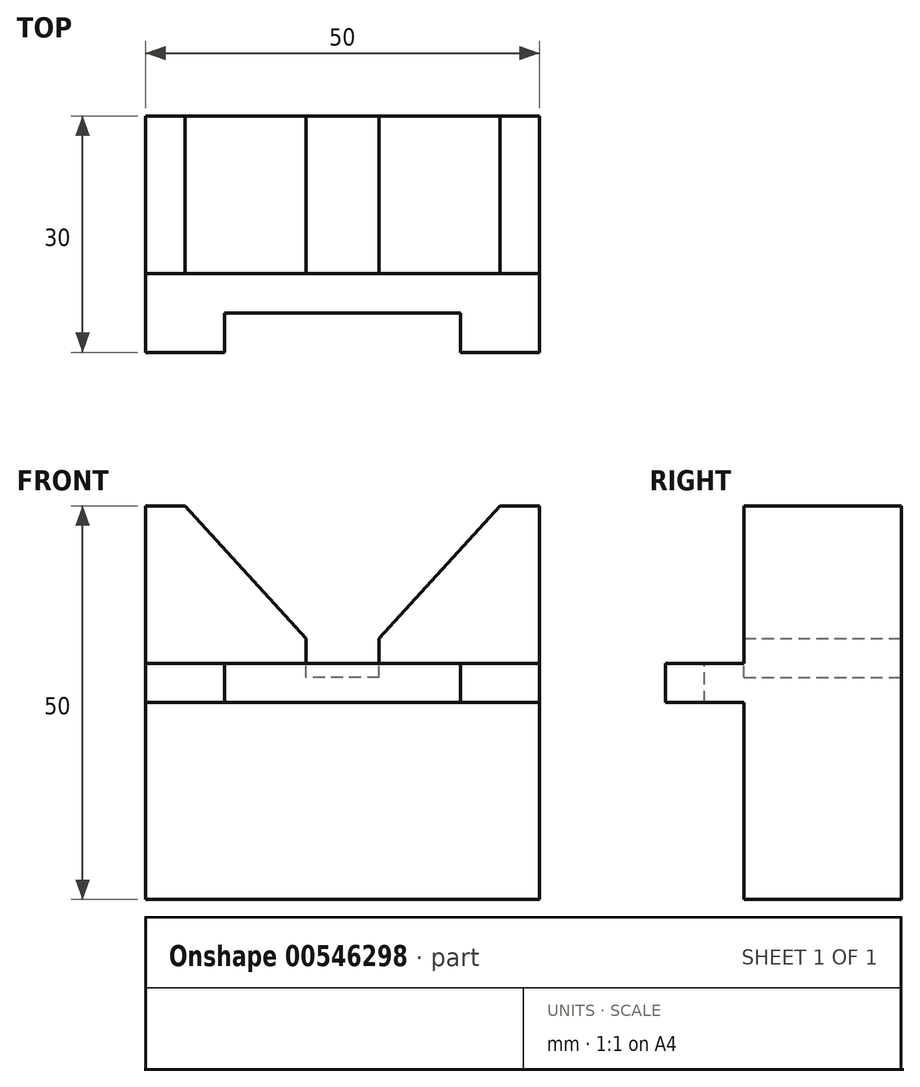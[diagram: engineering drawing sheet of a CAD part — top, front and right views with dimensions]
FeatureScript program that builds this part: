
annotation { "Feature Type Name" : "Feature", "Feature Type Description" : "" }
export const myFeature = defineFeature(function(context is Context, id is Id, definition is map)
    precondition{}
    {
        {
            var Q0;
            Q0=qCreatedBy(makeId("Top.planeOp"),FACE);
            var sketch = newSketch(context, id + "F0", { "sketchPlane" : qUnion([Q0])});
            skLineSegment(sketch, "E0.bottom", {"start": v(25, -15) * mm, "end": v(-25, -15) * mm});
            skLineSegment(sketch, "E0.top", {"start": v(25, 15) * mm, "end": v(-25, 15) * mm});
            skLineSegment(sketch, "E0.left", {"start": v(25, -15) * mm, "end": v(25, 15) * mm});
            skLineSegment(sketch, "E0.right", {"start": v(-25, -15) * mm, "end": v(-25, 15) * mm});
            skPoint(sketch, "E0.middle", {"position": v(0, 0) * mm});
            skSolve(sketch);
        }
        {
            var Q0;
            Q0 = qSketchRegion(id + "F0", true);
            extrude(context, id + "F1", {"entities" : qUnion([Q0]), "depth" : 50 * mm, "offsetDistance" : 25 * mm});
        }
        {
            var Q0;
            Q0=makeQuery(id+"F1.opExtrude","CAP_FACE",FACE,{"disambiguationData":[OSD([sQuery(id+"F0.wireOp",EDGE,"E0.bottom"),sQuery(id+"F0.wireOp",EDGE,"E0.top"),sQuery(id+"F0.wireOp",EDGE,"E0.left"),sQuery(id+"F0.wireOp",EDGE,"E0.right")])],"isStart":false});
            var sketch = newSketch(context, id + "F2", { "sketchPlane" : qUnion([Q0])});
            skLineSegment(sketch, "E1", {"start": v(-15, -15) * mm, "end": v(-15, -10) * mm});
            skLineSegment(sketch, "E2", {"start": v(-15, -10) * mm, "end": v(15, -10) * mm});
            skLineSegment(sketch, "E3", {"start": v(15, -10) * mm, "end": v(15, -15) * mm});
            skLineSegment(sketch, "E4", {"start": v(-25, -5) * mm, "end": v(25, -5) * mm});
            skSolve(sketch);
        }
        {
            var Q0;
            {var subQ2=sQuery(id+"F2.wireOp",EDGE,"E1");Q0=makeQuery(id+"F2.imprint","IMPRINT",FACE,{"disambiguationData":[TD([[makeQuery(id+"F2.imprint","IMPRINT",EDGE,{"derivedFrom":subQ2}),1.0]])]});}
            extrude(context, id + "F3", {"entities" : qUnion([Q0]), "operationType" : NewBodyOperationType.REMOVE, "oppositeDirection" : true, "depth" : 20 * mm, "offsetDistance" : 25 * mm});
        }
        {
            var Q0;
            {var subQ0=sQuery(id+"F0.wireOp",EDGE,"E0.bottom");Q0=makeQuery(id+"F3.boolean.opBoolean","SPLIT",FACE,{"disambiguationData":[TD([makeQuery(id+"F1.opExtrude","SWEPT_FACE",FACE,{"disambiguationData":[OSD([subQ0])]})])],"derivedFrom":makeQuery(id+"F1.opExtrude","CAP_FACE",FACE,{"disambiguationData":[OSD([subQ0,sQuery(id+"F0.wireOp",EDGE,"E0.top"),sQuery(id+"F0.wireOp",EDGE,"E0.left"),sQuery(id+"F0.wireOp",EDGE,"E0.right")])],"isStart":false})});}
            extrude(context, id + "F4", {"entities" : qUnion([Q0]), "operationType" : NewBodyOperationType.REMOVE, "endBound" : BoundingType.THROUGH_ALL, "oppositeDirection" : true, "depth" : 25 * mm, "offsetDistance" : 25 * mm});
        }
        {
            var Q0;
            Q0=makeQuery(id+"F1.opExtrude","CAP_FACE",FACE,{"disambiguationData":[OSD([sQuery(id+"F0.wireOp",EDGE,"E0.bottom"),sQuery(id+"F0.wireOp",EDGE,"E0.top"),sQuery(id+"F0.wireOp",EDGE,"E0.left"),sQuery(id+"F0.wireOp",EDGE,"E0.right")])],"isStart":true});
            var sketch = newSketch(context, id + "F5", { "sketchPlane" : qUnion([Q0])});
            skLineSegment(sketch, "E5", {"start": v(-25, 5) * mm, "end": v(25, 5) * mm});
            skSolve(sketch);
        }
        {
            var Q0;
            Q0 = qSketchRegion(id + "F5", true);
            var Q1;
            {var subQ6=sQuery(id+"F5.wireOp",EDGE,"E5");Q1=makeQuery(id+"F5.imprint","IMPRINT",FACE,{"disambiguationData":[TD([[makeQuery(id+"F5.imprint","IMPRINT",EDGE,{"derivedFrom":subQ6}),1.0]])]});}
            extrude(context, id + "F6", {"entities" : qUnion([Q0, Q1]), "operationType" : NewBodyOperationType.REMOVE, "oppositeDirection" : true, "depth" : 25 * mm, "offsetDistance" : 25 * mm});
        }
        {
            var Q0;
            Q0=makeQuery(id+"F1.opExtrude","SWEPT_FACE",FACE,{"disambiguationData":[OSD([sQuery(id+"F0.wireOp",EDGE,"E0.top")])]});
            var sketch = newSketch(context, id + "F7", { "sketchPlane" : qUnion([Q0])});
            skLineSegment(sketch, "E6", {"start": v(-25, 28.18) * mm, "end": v(-4.65, 28.18) * mm});
            skLineSegment(sketch, "E7.MirrorCS", {"start": v(25, 28.18) * mm, "end": v(4.65, 28.18) * mm});
            skLineSegment(sketch, "E8", {"start": v(-4.65, 28.18) * mm, "end": v(-4.65, 33.18) * mm});
            skLineSegment(sketch, "E9", {"start": v(-4.65, 33.18) * mm, "end": v(-20, 50) * mm});
            skLineSegment(sketch, "E10.MirrorCS", {"start": v(4.65, 28.18) * mm, "end": v(4.65, 33.18) * mm});
            skLineSegment(sketch, "E11.MirrorCS", {"start": v(4.65, 33.18) * mm, "end": v(20, 50) * mm});
            skLineSegment(sketch, "E12", {"start": v(-25, 28.18) * mm, "end": v(25, 28.18) * mm});
            skSolve(sketch);
        }
        {
            var Q0;
            {var subQ4=sQuery(id+"F7.wireOp",EDGE,"E8");Q0=makeQuery(id+"F7.imprint","IMPRINT",FACE,{"disambiguationData":[TD([[makeQuery(id+"F7.imprint","IMPRINT",EDGE,{"derivedFrom":subQ4}),-1.0]])]});}
            extrude(context, id + "F8", {"entities" : qUnion([Q0]), "operationType" : NewBodyOperationType.REMOVE, "oppositeDirection" : true, "depth" : 20 * mm, "offsetDistance" : 25 * mm});
        }
    });
